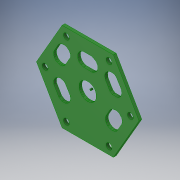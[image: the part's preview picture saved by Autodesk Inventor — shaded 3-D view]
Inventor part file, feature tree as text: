
AUTODESK INVENTOR PART (.ipt)
format: ipt  version: 2019.4 (Build 234330000, 330)  size: 215,040 bytes
history: native  units: mm
features: extrude x2, sketch x2, pattern_circular x1, imported_body x1
ambient origin geometry x8: Origin, YZ Plane, XZ Plane, XY Plane, X Axis, Y Axis, Z Axis, Center Point
bodies: Solid1 (feature_tree)
feature tree (6):
  extrude  "Extrusion1"  Depth=1.0mm TaperAngle=0.0deg
  extrude  "Extrusion2"  Depth=3.5mm
  pattern_circular  "Circular Pattern1"  [2 undecoded]
  sketch  "Sketch1"  dims[d0=1.0mm d1=1.0mm d2=0.0mm]
  sketch  "Sketch2"  dims[d3=25.0mm d4=3.5mm d5=2.0mm d6=0.0mm d7=60.0mm d8=62.831853mm]
  imported_body  "Base1"
note: 2 required parameter values undecoded (feature->parameter linkage not recoverable at this tier; creation-order binding heuristic only, values carry confidence <= 0.55)
